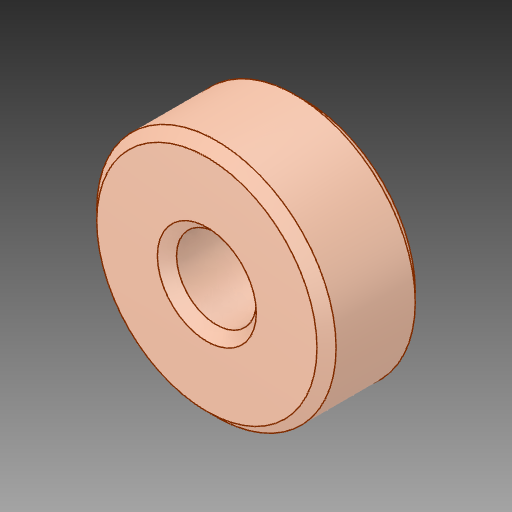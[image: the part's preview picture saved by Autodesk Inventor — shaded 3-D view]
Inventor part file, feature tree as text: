
AUTODESK INVENTOR PART (.ipt)
format: ipt  version: 2018 (Build 220112000, 112)  size: 122,880 bytes
history: native  units: mm
features: other x1, chamfer x1
ambient origin geometry x8: Origin, YZ Plane, XZ Plane, XY Plane, X Axis, Y Axis, Z Axis, Center Point
bodies: Body1 (feature_tree)
feature tree (2):
  other  "ソリッド1"
  chamfer  "Chamfer1"  [1 undecoded]
note: 1 required parameter value undecoded (feature->parameter linkage not recoverable at this tier; creation-order binding heuristic only, values carry confidence <= 0.55)
